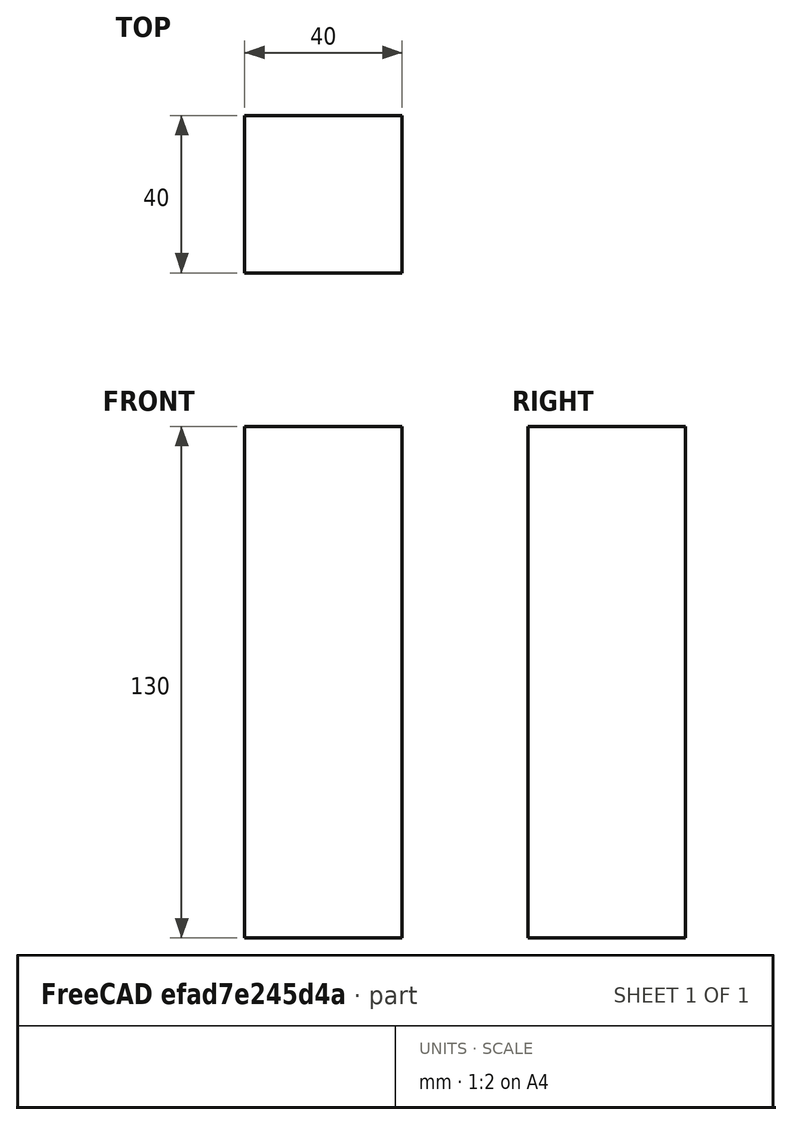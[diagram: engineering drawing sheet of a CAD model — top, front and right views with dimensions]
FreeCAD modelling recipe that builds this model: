
FCSTD DOCUMENT  (FreeCAD 0.16R6707 (Git))
Label: batterie
License: All rights reserved
LicenseURL: http://en.wikipedia.org/wiki/All_rights_reserved
objects: Sketcher::SketchObject×1, PartDesign::Pad×1
note: 3 computed .brp shape members not serialized (recipe doc carries the construction recipe); baked Part::Feature solids carry a one-line shape summary decoded from their .brp

FEATURE [Sketcher::SketchObject] Sketch
  sketch-geometry (4):
    g0: LineSegment StartX=0 StartY=0 StartZ=0 EndX=40 EndY=0 EndZ=0
    g1: LineSegment StartX=40 StartY=0 StartZ=0 EndX=40 EndY=40 EndZ=0
    g2: LineSegment StartX=40 StartY=40 StartZ=0 EndX=0 EndY=40 EndZ=0
    g3: LineSegment StartX=0 StartY=40 StartZ=0 EndX=0 EndY=0 EndZ=0
  constraints (11):
    c: Coincident(g0,g1)
    c: Coincident(g1,g2)
    c: Coincident(g2,g3)
    c: Coincident(g3,g0)
    c: Horizontal(g0)
    c: Horizontal(g2)
    c: Vertical(g1)
    c: Vertical(g3)
    c: Coincident(g0,g-1)
    c: Distance(g3) = 40
    c: Distance(g2) = 40
FEATURE [PartDesign::Pad] Pad
  Length = 130
  Length2 = 100
  Sketch = -> Sketch
  Type = 0
